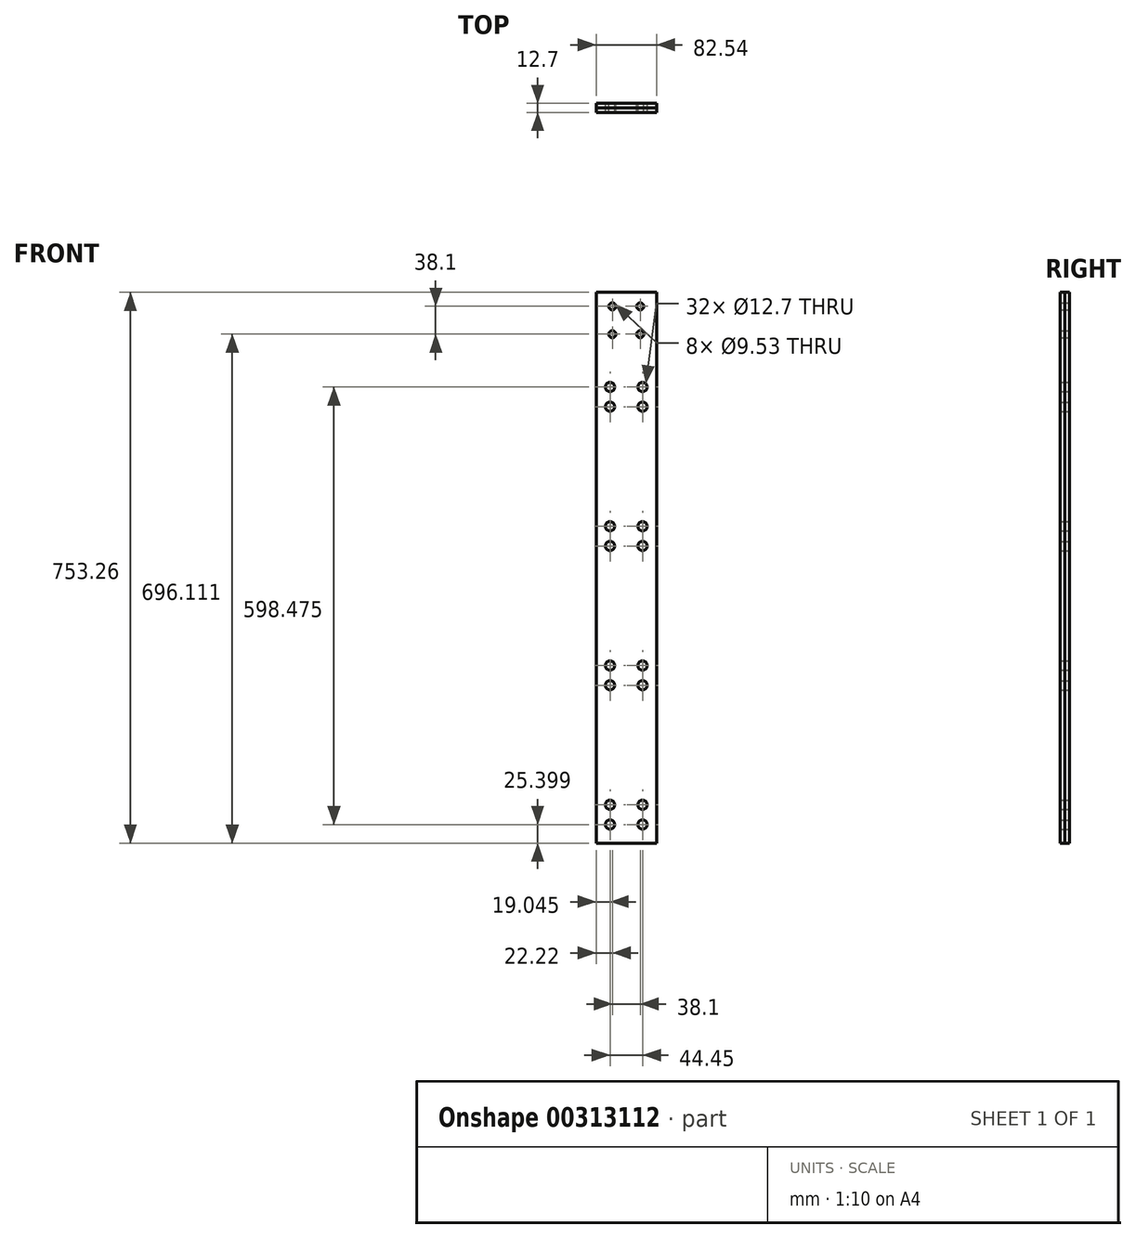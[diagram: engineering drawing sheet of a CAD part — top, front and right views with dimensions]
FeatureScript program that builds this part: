
annotation { "Feature Type Name" : "Feature", "Feature Type Description" : "" }
export const myFeature = defineFeature(function(context is Context, id is Id, definition is map)
    precondition{}
    {
        {
            var Q0;
            Q0=qCreatedBy(makeId("Front.planeOp"),FACE);
            var sketch = newSketch(context, id + "F0", { "sketchPlane" : qUnion([Q0])});
            skLineSegment(sketch, "E0.bottom", {"start": v(-41.28, 376.63) * mm, "end": v(41.28, 376.63) * mm});
            skLineSegment(sketch, "E0.top", {"start": v(-41.28, -376.63) * mm, "end": v(41.28, -376.63) * mm});
            skLineSegment(sketch, "E0.left", {"start": v(-41.28, 376.63) * mm, "end": v(-41.28, -376.63) * mm});
            skLineSegment(sketch, "E0.right", {"start": v(41.28, 376.63) * mm, "end": v(41.28, -376.63) * mm});
            skPoint(sketch, "E0.middle", {"position": v(0, 0) * mm});
            skSolve(sketch);
        }
        {
            var Q0;
            Q0=makeQuery(id+"F0.imprint","IMPRINT",FACE,{"disambiguationData":[TD([[makeQuery(id+"F0.imprint","IMPRINT",EDGE,{"derivedFrom":sQuery(id+"F0.wireOp",EDGE,"E0.bottom")}),-1.0]])]});
            extrude(context, id + "F1", {"entities" : qUnion([Q0]), "oppositeDirection" : true, "depth" : 6.35 * mm});
        }
        {
            var Q0;
            Q0=makeQuery(id+"F1.opExtrude","CAP_FACE",FACE,{"disambiguationData":[OSD([sQuery(id+"F0.wireOp",EDGE,"E0.bottom"),sQuery(id+"F0.wireOp",EDGE,"E0.top"),sQuery(id+"F0.wireOp",EDGE,"E0.left"),sQuery(id+"F0.wireOp",EDGE,"E0.right")])],"isStart":true});
            var sketch = newSketch(context, id + "F2", { "sketchPlane" : qUnion([Q0])});
            skLineSegment(sketch, "E1.bottom", {"start": v(-41.28, 376.63) * mm, "end": v(41.27, 376.63) * mm});
            skLineSegment(sketch, "E1.top", {"start": v(-41.27, -376.63) * mm, "end": v(41.28, -376.63) * mm});
            skLineSegment(sketch, "E1.left", {"start": v(-41.28, 376.63) * mm, "end": v(-41.27, -376.63) * mm});
            skLineSegment(sketch, "E1.right", {"start": v(41.27, 376.63) * mm, "end": v(41.28, -376.63) * mm});
            skSolve(sketch);
        }
        {
            var Q0;
            Q0 = qSketchRegion(id + "F2", true);
            extrude(context, id + "F3", {"entities" : qUnion([Q0]), "depth" : 6.35 * mm});
        }
        {
            var Q0;
            Q0=makeQuery(id+"F1.opExtrude","CAP_FACE",FACE,{"disambiguationData":[OSD([sQuery(id+"F0.wireOp",EDGE,"E0.bottom"),sQuery(id+"F0.wireOp",EDGE,"E0.top"),sQuery(id+"F0.wireOp",EDGE,"E0.left"),sQuery(id+"F0.wireOp",EDGE,"E0.right")])],"isStart":false});
            var sketch = newSketch(context, id + "F4", { "sketchPlane" : qUnion([Q0])});
            skCircle(sketch, "E2", {"center": v(-19.05, 357.58) * mm, "radius": 4.76 * mm});
            skCircle(sketch, "E3", {"center": v(19.05, 357.58) * mm, "radius": 4.76 * mm});
            skCircle(sketch, "E4", {"center": v(19.05, 319.48) * mm, "radius": 4.76 * mm});
            skCircle(sketch, "E5", {"center": v(-19.05, 319.48) * mm, "radius": 4.76 * mm});
            skLineSegment(sketch, "E6", {"start": v(-19.05, 357.58) * mm, "end": v(19.05, 357.58) * mm, "construction": true});
            skPoint(sketch, "E7", {"position": v(0, 357.58) * mm});
            skCircle(sketch, "E8.2.1.0", {"center": v(22.23, -351.23) * mm, "radius": 6.35 * mm});
            skCircle(sketch, "E9", {"center": v(22.23, -324.26) * mm, "radius": 6.35 * mm});
            skCircle(sketch, "E10.0.1.0", {"center": v(22.23, -133.76) * mm, "radius": 6.35 * mm});
            skCircle(sketch, "E10.0.1.1", {"center": v(22.23, -160.73) * mm, "radius": 6.35 * mm});
            skCircle(sketch, "E10.0.2.0", {"center": v(22.23, 56.74) * mm, "radius": 6.35 * mm});
            skCircle(sketch, "E10.0.2.1", {"center": v(22.23, 29.77) * mm, "radius": 6.35 * mm});
            skCircle(sketch, "E10.0.3.0", {"center": v(22.23, 247.24) * mm, "radius": 6.35 * mm});
            skCircle(sketch, "E10.0.3.1", {"center": v(22.23, 220.27) * mm, "radius": 6.35 * mm});
            skCircle(sketch, "E10.1.0.0", {"center": v(-22.22, -324.26) * mm, "radius": 6.35 * mm});
            skCircle(sketch, "E10.1.0.1", {"center": v(-22.22, -351.23) * mm, "radius": 6.35 * mm});
            skCircle(sketch, "E10.1.1.0", {"center": v(-22.22, -133.76) * mm, "radius": 6.35 * mm});
            skCircle(sketch, "E10.1.1.1", {"center": v(-22.22, -160.73) * mm, "radius": 6.35 * mm});
            skCircle(sketch, "E10.1.2.0", {"center": v(-22.22, 56.74) * mm, "radius": 6.35 * mm});
            skCircle(sketch, "E10.1.2.1", {"center": v(-22.22, 29.77) * mm, "radius": 6.35 * mm});
            skCircle(sketch, "E10.1.3.0", {"center": v(-22.22, 247.24) * mm, "radius": 6.35 * mm});
            skCircle(sketch, "E10.1.3.1", {"center": v(-22.22, 220.27) * mm, "radius": 6.35 * mm});
            skLineSegment(sketch, "E10.direction1", {"start": v(22.23, -351.23) * mm, "end": v(-22.22, -351.23) * mm, "construction": true});
            skLineSegment(sketch, "E10.direction2", {"start": v(22.23, -351.23) * mm, "end": v(22.23, -160.73) * mm, "construction": true});
            skSolve(sketch);
        }
        {
            var Q0;
            Q0 = qSketchRegion(id + "F4", true);
            extrude(context, id + "F5", {"entities" : qUnion([Q0]), "operationType" : NewBodyOperationType.REMOVE, "endBound" : BoundingType.THROUGH_ALL, "oppositeDirection" : true, "depth" : 25.4 * mm});
        }
    });
